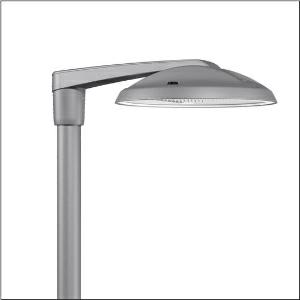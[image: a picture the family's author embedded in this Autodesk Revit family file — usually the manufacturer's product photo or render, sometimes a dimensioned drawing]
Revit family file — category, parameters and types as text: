
# Revit family: dl_r__50_mini___st1_0a_5xa248d33s08le_e5ac
name_source: partatom
category: Lighting Fixtures
units: mm (PartAtom-declared; Revit-internal decimal feet)

## family parameters
Cut with Voids When Loaded = No
Host = Face
Light Source = No
Part Type = Normal
Room Calculation Point = No
Round Connector Dimension = Use Diameter
Shared = No

## types (1)
- --- (1 x LED, 10040 lm, 66.3 W, 3000K)
    Apparent Load = 66 VA
    CIE Flux Codes = 37 72 97 100 100
    Color Rendering = 70
    Color Temperature = 3000K
    Default Elevation = 1800 mm
    Description = DL® 50 mini, mast luminaire, primary light control with lens, of PMMA, primary optical cover: cover, of toughened safety glass, transparent, light distribution: ST1.0a, light emission: direct distribution, primary light characteristic: asymmetric, installation type: post-top, side-entry, LED, High Power LED, rated luminous flux: 10.040lm, luminous efficacy: 152lm/W, light colour: 730, colour temperature: 3000K, control gear: D4i, control: overheat protection, constant luminous flux control, time-dependent luminous flux control, flexible luminous flux parameterisation, mains connection: 230..240V, AC, 50/60Hz, connection cable pre-assembled, cable length: 8,5m, start of lifetime: 66W, end of service life: 68W, reduction: 32W, luminaire housing, of diecast aluminium, powder-coated, Siteco® metallic grey (DB 702S), inclination adjustable: 0°, 5°, 10° (post-top) | 0°, -5°, -10°, -15° (side-entry), please order mast post-top element or mast side-entry element separately, diameter: 500mm, height: 115mm, post-top: for spigot size d x l = 76 x 100mm; with reducer (optional accessory) 60 x 100mm | side-entry: for spigot size d x l = 60 x 100mm; with reducer (optional accessory) 42 x 100mm, mounting height: 4..6m, Smart Interface above, protection rating (complete): IP66, insulation class (complete): insulation class II (safety insulation), certification: CE, ENEC, ENEC+, VDE, impact resistance: IK08, permissible operating ambient temperature for outdoor applications: -25..+40°C, standard-compliant lighting for roads and squares, packaging unit: 1 piece

Light Distribution: ST1.0a
    Height = 115 mm
    Lamp = 1 x LED
    Lamp Light Flux = 10040 lm
    Lamp Power = 66.3 W
    Lamp count = 1
    Length = 500 mm
    Luminous efficacy = 151 lm/W
    Manufacturer = Siteco
    ModVariant = No
    Model = 5XA248D33S08LE
    Number of Poles = 1
    OnlyDefault = Yes
    Power Factor = 1
    Product Name = DL® 50 mini | ST1.0a
    Product group = mast luminaire | pylon top
    ProductGroupID = 6100
    Protection Class = Protection class II
    Protection Degree = IP 66
    RLX_Detail_Level = 1
    RLX_Emergency_Light_Flux = 0 lm
    RLX_Emergency_Type = 0
    RLX_Emergency_Type_DB = No
    RlxData = <blob elided: 106205 chars, md5=dbe77333>
    Socket = socket
    Standby Power = 0 W
    System Light Flux = 10040 lm
    System Power = 66 W
    Type Comments = factory setting: luminous flux: 100 % | dim-lin: 254 | 691 mA
    Type Image = l_1251788.jpg
    URL = http://relux.com
    VarID = @adj_038171
    Voltage = 0 V
    Weight = 0.00 kg
    Width = 0 mm  [stored 0 ft]

note: [stored X ft] marks values corroborated as IEEE doubles in the binary element streams (Revit-internal decimal feet)

## geometry (parser evidence)
native form markers: Blend x4, Sweep x9
no freeform markers — native parametric forms only
